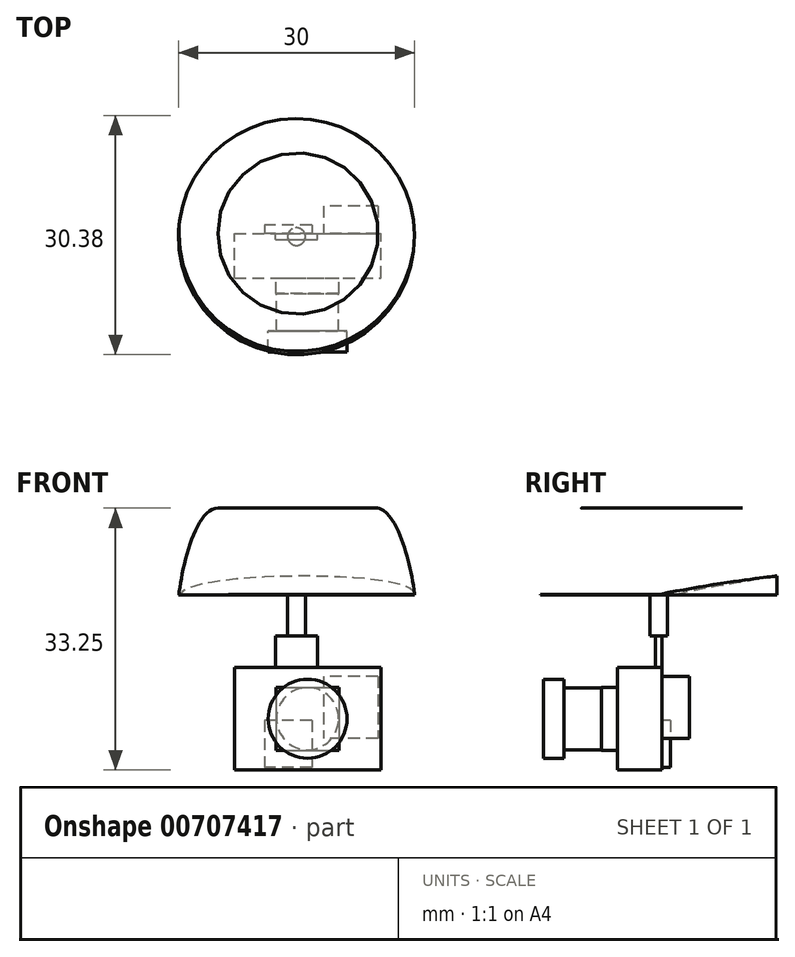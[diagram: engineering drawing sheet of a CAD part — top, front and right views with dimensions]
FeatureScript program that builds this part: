
annotation { "Feature Type Name" : "Feature", "Feature Type Description" : "" }
export const myFeature = defineFeature(function(context is Context, id is Id, definition is map)
    precondition{}
    {
        {
            var Q0;
            Q0=qCreatedBy(makeId("Front.planeOp"),FACE);
            var sketch = newSketch(context, id + "F0", { "sketchPlane" : qUnion([Q0])});
            skLineSegment(sketch, "E0.bottom", {"start": v(-9.3, 13) * mm, "end": v(9.3, 13) * mm});
            skLineSegment(sketch, "E0.top", {"start": v(-9.3, 0) * mm, "end": v(9.3, 0) * mm});
            skLineSegment(sketch, "E0.left", {"start": v(-9.3, 13) * mm, "end": v(-9.3, 0) * mm});
            skLineSegment(sketch, "E0.right", {"start": v(9.3, 13) * mm, "end": v(9.3, 0) * mm});
            skSolve(sketch);
        }
        {
            var Q0;
            Q0 = qSketchRegion(id + "F0", true);
            extrude(context, id + "F1", {"entities" : qUnion([Q0]), "depth" : 5.65 * mm, "offsetDistance" : 25 * mm});
        }
        {
            var Q0;
            Q0=makeQuery(id+"F1.opExtrude","CAP_FACE",FACE,{"disambiguationData":[OSD([sQuery(id+"F0.wireOp",EDGE,"E0.bottom"),sQuery(id+"F0.wireOp",EDGE,"E0.top"),sQuery(id+"F0.wireOp",EDGE,"E0.left"),sQuery(id+"F0.wireOp",EDGE,"E0.right")])],"isStart":false});
            var sketch = newSketch(context, id + "F2", { "sketchPlane" : qUnion([Q0])});
            skLineSegment(sketch, "E1.bottom", {"start": v(-4, 10.5) * mm, "end": v(4, 10.5) * mm});
            skLineSegment(sketch, "E1.top", {"start": v(-4, 2.5) * mm, "end": v(4, 2.5) * mm});
            skLineSegment(sketch, "E1.left", {"start": v(-4, 10.5) * mm, "end": v(-4, 2.5) * mm});
            skLineSegment(sketch, "E1.right", {"start": v(4, 10.5) * mm, "end": v(4, 2.5) * mm});
            skSolve(sketch);
        }
        {
            var Q0;
            Q0=makeQuery(id+"F2.imprint","IMPRINT",FACE,{"disambiguationData":[TD([[makeQuery(id+"F2.imprint","IMPRINT",EDGE,{"derivedFrom":sQuery(id+"F2.wireOp",EDGE,"E1.bottom")}),-1.0]])]});
            extrude(context, id + "F3", {"entities" : qUnion([Q0]), "operationType" : NewBodyOperationType.ADD, "depth" : 2 * mm, "offsetDistance" : 25 * mm});
        }
        {
            var Q0;
            Q0=makeQuery(id+"F3.opExtrude","CAP_FACE",FACE,{"disambiguationData":[OSD([sQuery(id+"F2.wireOp",EDGE,"E1.bottom"),sQuery(id+"F2.wireOp",EDGE,"E1.top"),sQuery(id+"F2.wireOp",EDGE,"E1.left"),sQuery(id+"F2.wireOp",EDGE,"E1.right")])],"isStart":false});
            var sketch = newSketch(context, id + "F4", { "sketchPlane" : qUnion([Q0])});
            skLineSegment(sketch, "E2", {"start": v(-4, 10.5) * mm, "end": v(4, 2.5) * mm, "construction": true});
            skLineSegment(sketch, "E3", {"start": v(4, 10.5) * mm, "end": v(-4, 2.5) * mm, "construction": true});
            skCircle(sketch, "E4", {"center": v(0, 6.5) * mm, "radius": 3.95 * mm});
            skSolve(sketch);
        }
        {
            var Q0;
            Q0=makeQuery(id+"F4.imprint","IMPRINT",FACE,{"disambiguationData":[TD([[makeQuery(id+"F4.imprint","IMPRINT",EDGE,{"derivedFrom":sQuery(id+"F4.wireOp",EDGE,"E4")}),1.0]])]});
            extrude(context, id + "F5", {"entities" : qUnion([Q0]), "operationType" : NewBodyOperationType.ADD, "depth" : 4.75 * mm, "offsetDistance" : 25 * mm});
        }
        {
            var Q0;
            Q0=makeQuery(id+"F5.opExtrude","CAP_FACE",FACE,{"disambiguationData":[OSD([sQuery(id+"F4.wireOp",EDGE,"E4")])],"isStart":false});
            var sketch = newSketch(context, id + "F6", { "sketchPlane" : qUnion([Q0])});
            skCircle(sketch, "E5.0", {"center": v(0, 6.5) * mm, "radius": 3.95 * mm});
            skCircle(sketch, "E6", {"center": v(0, 6.5) * mm, "radius": 5 * mm});
            skSolve(sketch);
        }
        {
            var Q0;
            Q0 = qSketchRegion(id + "F6", true);
            var Q1;
            Q1=makeQuery(id+"F6.imprint","IMPRINT",FACE,{"disambiguationData":[TD([[makeQuery(id+"F6.imprint","IMPRINT",EDGE,{"derivedFrom":sQuery(id+"F6.wireOp",EDGE,"E5.0")}),1.0]])]});
            extrude(context, id + "F7", {"entities" : qUnion([Q0, Q1]), "operationType" : NewBodyOperationType.ADD, "depth" : 2.65 * mm, "offsetDistance" : 25 * mm});
        }
        {
            var Q0;
            Q0=makeQuery(id+"F1.opExtrude","CAP_FACE",FACE,{"disambiguationData":[OSD([sQuery(id+"F0.wireOp",EDGE,"E0.bottom"),sQuery(id+"F0.wireOp",EDGE,"E0.top"),sQuery(id+"F0.wireOp",EDGE,"E0.left"),sQuery(id+"F0.wireOp",EDGE,"E0.right")])],"isStart":true});
            var sketch = newSketch(context, id + "F8", { "sketchPlane" : qUnion([Q0])});
            skLineSegment(sketch, "E7.bottom", {"start": v(-8.94, 11.9) * mm, "end": v(-2.04, 11.9) * mm});
            skLineSegment(sketch, "E7.top", {"start": v(-8.94, 4) * mm, "end": v(-2.04, 4) * mm});
            skLineSegment(sketch, "E7.left", {"start": v(-8.94, 11.9) * mm, "end": v(-8.94, 4) * mm});
            skLineSegment(sketch, "E7.right", {"start": v(-2.04, 11.9) * mm, "end": v(-2.04, 4) * mm});
            skLineSegment(sketch, "E8.bottom", {"start": v(-0.54, 6.32) * mm, "end": v(5.48, 6.32) * mm});
            skLineSegment(sketch, "E8.top", {"start": v(-0.54, 0.3) * mm, "end": v(5.48, 0.3) * mm});
            skLineSegment(sketch, "E8.left", {"start": v(-0.54, 6.32) * mm, "end": v(-0.54, 0.3) * mm});
            skLineSegment(sketch, "E8.right", {"start": v(5.48, 6.32) * mm, "end": v(5.48, 0.3) * mm});
            skSolve(sketch);
        }
        {
            var Q0;
            Q0=makeQuery(id+"F8.imprint","IMPRINT",FACE,{"disambiguationData":[TD([[makeQuery(id+"F8.imprint","IMPRINT",EDGE,{"derivedFrom":sQuery(id+"F8.wireOp",EDGE,"E7.bottom")}),-1.0]])]});
            extrude(context, id + "F9", {"entities" : qUnion([Q0]), "operationType" : NewBodyOperationType.ADD, "depth" : 3.5 * mm, "offsetDistance" : 25 * mm});
        }
        {
            var Q0;
            Q0=makeQuery(id+"F8.imprint","IMPRINT",FACE,{"disambiguationData":[TD([[makeQuery(id+"F8.imprint","IMPRINT",EDGE,{"derivedFrom":sQuery(id+"F8.wireOp",EDGE,"E8.bottom")}),-1.0]])]});
            extrude(context, id + "F10", {"entities" : qUnion([Q0]), "operationType" : NewBodyOperationType.ADD, "depth" : 1.07 * mm, "offsetDistance" : 25 * mm});
        }
        {
            var Q0;
            Q0=makeQuery(id+"F8.imprint","IMPRINT",FACE,{"disambiguationData":[TD([[makeQuery(id+"F8.imprint","IMPRINT",EDGE,{"derivedFrom":sQuery(id+"F8.wireOp",EDGE,"E7.bottom")}),1.0]])]});
            var sketch = newSketch(context, id + "F11", { "sketchPlane" : qUnion([Q0])});
            skLineSegment(sketch, "E9.bottom", {"start": v(4.05, 13) * mm, "end": v(-1.25, 13) * mm});
            skLineSegment(sketch, "E9.top", {"start": v(4.05, 17) * mm, "end": v(-1.25, 17) * mm});
            skLineSegment(sketch, "E9.left", {"start": v(4.05, 13) * mm, "end": v(4.05, 17) * mm});
            skLineSegment(sketch, "E9.right", {"start": v(-1.25, 13) * mm, "end": v(-1.25, 17) * mm});
            skSolve(sketch);
        }
        {
            var Q0;
            Q0 = qSketchRegion(id + "F11", true);
            extrude(context, id + "F12", {"entities" : qUnion([Q0]), "operationType" : NewBodyOperationType.ADD, "oppositeDirection" : true, "depth" : .8 * mm, "offsetDistance" : 25 * mm});
        }
        {
            var Q0;
            Q0=makeQuery(id+"F12.opExtrude","SWEPT_FACE",FACE,{"disambiguationData":[OSD([sQuery(id+"F11.wireOp",EDGE,"E9.top")])]});
            var sketch = newSketch(context, id + "F13", { "sketchPlane" : qUnion([Q0])});
            skLineSegment(sketch, "E10", {"start": v(1.25, -0.8) * mm, "end": v(-4.05, 0) * mm, "construction": true});
            skLineSegment(sketch, "E11", {"start": v(-4.05, -0.8) * mm, "end": v(1.25, 0) * mm, "construction": true});
            skCircle(sketch, "E12", {"center": v(-1.4, -0.4) * mm, "radius": 1.13 * mm});
            skSolve(sketch);
        }
        {
            var Q0;
            {var subQ0=sQuery(id+"F13.wireOp",EDGE,"E12");var subQ1=makeQuery(id+"F12.opExtrude","CAP_EDGE",EDGE,{"disambiguationData":[OSD([sQuery(id+"F11.wireOp",EDGE,"E9.top")])],"isStart":true});var subQ2=makeQuery(id+"F13.imprint","INTERSECT",VERTEX,{"disambiguationData":[OD(0.0)],"derivedFrom":[subQ1,subQ0]});Q0=makeQuery(id+"F13.imprint","IMPRINT",FACE,{"disambiguationData":[TD([[makeQuery(id+"F13.imprint","IMPRINT",EDGE,{"disambiguationData":[TD([[subQ2,1.0]])],"derivedFrom":subQ0}),1.0]])]});}
            var Q1;
            {var subQ0=sQuery(id+"F13.wireOp",EDGE,"E12");var subQ1=sQuery(id+"F11.wireOp",EDGE,"E9.top");var subQ2=makeQuery(id+"F12.opExtrude","CAP_EDGE",EDGE,{"disambiguationData":[OSD([subQ1])],"isStart":true});var subQ3=makeQuery(id+"F13.imprint","INTERSECT",VERTEX,{"disambiguationData":[OD(0.0)],"derivedFrom":[subQ2,subQ0]});Q1=makeQuery(id+"F13.imprint","IMPRINT",FACE,{"disambiguationData":[TD([[makeQuery(id+"F13.imprint","IMPRINT",EDGE,{"disambiguationData":[TD([[subQ3,-1.0]])],"derivedFrom":subQ0}),1.0]])]});}
            var Q2;
            {var subQ0=sQuery(id+"F13.wireOp",EDGE,"E12");var subQ1=makeQuery(id+"F12.opExtrude","CAP_EDGE",EDGE,{"disambiguationData":[OSD([sQuery(id+"F11.wireOp",EDGE,"E9.top")])],"isStart":false});var subQ2=makeQuery(id+"F13.imprint","INTERSECT",VERTEX,{"disambiguationData":[OD(0.0)],"derivedFrom":[subQ1,subQ0]});Q2=makeQuery(id+"F13.imprint","IMPRINT",FACE,{"disambiguationData":[TD([[makeQuery(id+"F13.imprint","IMPRINT",EDGE,{"disambiguationData":[TD([[subQ2,-1.0]])],"derivedFrom":subQ0}),1.0]])]});}
            extrude(context, id + "F14", {"entities" : qUnion([Q0, Q1, Q2]), "operationType" : NewBodyOperationType.ADD, "surfaceOperationType" : NewSurfaceOperationType.ADD, "depth" : 5.25 * mm, "offsetDistance" : 25 * mm});
        }
        {
            var Q0;
            Q0=makeQuery(id+"F14.opExtrude","CAP_FACE",FACE,{"disambiguationData":[OSD([sQuery(id+"F13.wireOp",EDGE,"E12")])],"isStart":false});
            var sketch = newSketch(context, id + "F15", { "sketchPlane" : qUnion([Q0])});
            skCircle(sketch, "E13.0", {"center": v(-1.4, -0.4) * mm, "radius": 1.13 * mm});
            skCircle(sketch, "E14", {"center": v(-1.4, -0.4) * mm, "radius": 15 * mm});
            skSolve(sketch);
        }
        {
            var Q0;
            Q0=makeQuery(id+"F15.imprint","IMPRINT",FACE,{"disambiguationData":[TD([[makeQuery(id+"F15.imprint","IMPRINT",EDGE,{"derivedFrom":sQuery(id+"F15.wireOp",EDGE,"E13.0")}),-1.0]])]});
            var Q1;
            Q1=makeQuery(id+"F15.imprint","IMPRINT",FACE,{"disambiguationData":[TD([[makeQuery(id+"F15.imprint","IMPRINT",EDGE,{"derivedFrom":sQuery(id+"F15.wireOp",EDGE,"E13.0")}),1.0]])]});
            extrude(context, id + "F16", {"entities" : qUnion([Q0, Q1]), "operationType" : NewBodyOperationType.ADD, "depth" : 11 * mm, "offsetDistance" : 25 * mm});
        }
        {
            var Q0;
            Q0=makeQuery(id+"F16.opExtrude","CAP_FACE",FACE,{"disambiguationData":[OSD([sQuery(id+"F15.wireOp",EDGE,"E14")])],"isStart":false});
            var sketch = newSketch(context, id + "F17", { "sketchPlane" : qUnion([Q0])});
            skSolve(sketch);
        }
        {
            var Q0;
            Q0=makeQuery(id+"F17.imprint","IMPRINT",FACE,{"disambiguationData":[TD([[makeQuery(id+"F17.imprint","IMPRINT",EDGE,{"derivedFrom":makeQuery(id+"F16.opExtrude","CAP_EDGE",EDGE,{"disambiguationData":[OSD([sQuery(id+"F15.wireOp",EDGE,"E14")])],"isStart":false})}),1.0]])]});
            var sketch = newSketch(context, id + "F18", { "sketchPlane" : qUnion([Q0])});
            skCircle(sketch, "E15.0", {"center": v(-1.4, -0.4) * mm, "radius": 15 * mm});
            skCircle(sketch, "E16", {"center": v(-1.4, -0.4) * mm, "radius": 10 * mm});
            skSolve(sketch);
        }
        {
            var Q0;
            Q0=qCreatedBy(makeId("Front.planeOp"),FACE);
            var sketch = newSketch(context, id + "F19", { "sketchPlane" : qUnion([Q0])});
            skLineSegment(sketch, "E17.0", {"start": v(-11.4, 33.25) * mm, "end": v(8.6, 33.25) * mm});
            skLineSegment(sketch, "E18.0", {"start": v(-16.35, 22.25) * mm, "end": v(13.6, 22.25) * mm});
            skFitSpline(sketch, "E19", {"points": [v(-16.35, 22.25) * mm, v(-11.4, 33.25) * mm], "startDerivative": vector(1.19, 9.9) * mm, "endDerivative": vector(8.78, 0.03) * mm});
            skLineSegment(sketch, "E20", {"start": v(-1.4, 33.25) * mm, "end": v(-1.38, 22.25) * mm, "construction": true});
            skLineSegment(sketch, "E21", {"start": v(-11.4, 33.25) * mm, "end": v(-18.37, 34.48) * mm});
            skLineSegment(sketch, "E22", {"start": v(-18.37, 34.48) * mm, "end": v(-17.27, 22.25) * mm});
            skLineSegment(sketch, "E23.0", {"start": v(-16.4, 33.25) * mm, "end": v(13.6, 33.25) * mm});
            skLineSegment(sketch, "E24", {"start": v(-16.35, 22.25) * mm, "end": v(-17.27, 22.25) * mm});
            skSolve(sketch);
        }
        {
            var Q0;
            {var subQ0=sQuery(id+"F19.wireOp",EDGE,"E19");Q0=makeQuery(id+"F19.imprint","IMPRINT",FACE,{"disambiguationData":[TD([[makeQuery(id+"F19.imprint","IMPRINT",EDGE,{"derivedFrom":subQ0}),1.0]])]});}
            var Q1;
            Q1=sQuery(id+"F19.wireOp",EDGE,"E20");
            revolve(context, id + "F20", {"operationType" : NewBodyOperationType.REMOVE, "surfaceOperationType" : NewSurfaceOperationType.NEW, "entities" : qUnion([Q0]), "axis" : qUnion([Q1]), "revolveType" : RevolveType.FULL, "oppositeDirection" : true});
        }
    });
